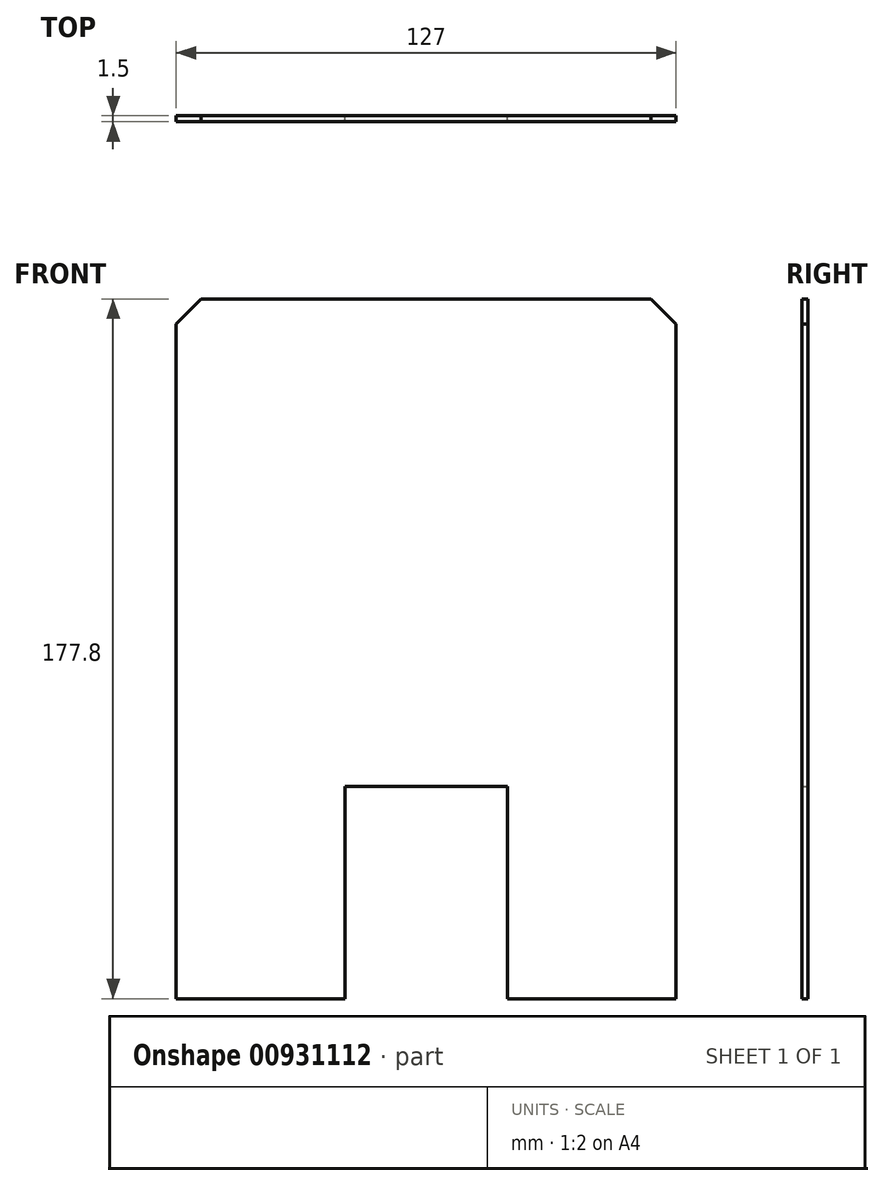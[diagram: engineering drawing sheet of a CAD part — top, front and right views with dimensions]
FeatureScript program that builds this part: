
annotation { "Feature Type Name" : "Feature", "Feature Type Description" : "" }
export const myFeature = defineFeature(function(context is Context, id is Id, definition is map)
    precondition{}
    {
        {
            var Q0;
            Q0=qCreatedBy(makeId("Front.planeOp"),FACE);
            var sketch = newSketch(context, id + "F0", { "sketchPlane" : qUnion([Q0])});
            skLineSegment(sketch, "E0.bottom", {"start": v(63.5, 88.9) * mm, "end": v(-63.5, 88.9) * mm});
            skLineSegment(sketch, "E0.top", {"start": v(63.5, -88.9) * mm, "end": v(20.64, -88.9) * mm});
            skLineSegment(sketch, "E0.left", {"start": v(63.5, 88.9) * mm, "end": v(63.5, -88.9) * mm});
            skLineSegment(sketch, "E0.right", {"start": v(-63.5, 88.9) * mm, "end": v(-63.5, -88.9) * mm});
            skPoint(sketch, "E0.middle", {"position": v(0, 0) * mm});
            skLineSegment(sketch, "E1.top", {"start": v(-20.64, -34.93) * mm, "end": v(20.64, -34.93) * mm});
            skLineSegment(sketch, "E1.left", {"start": v(-20.64, -88.9) * mm, "end": v(-20.64, -34.93) * mm});
            skLineSegment(sketch, "E1.right", {"start": v(20.64, -88.9) * mm, "end": v(20.64, -34.93) * mm});
            skLineSegment(sketch, "E2.trimOffspring", {"start": v(-20.64, -88.9) * mm, "end": v(-63.5, -88.9) * mm});
            skSolve(sketch);
        }
        {
            var Q0;
            Q0 = qSketchRegion(id + "F0", true);
            extrude(context, id + "F1", {"entities" : qUnion([Q0]), "endBound" : BoundingType.SYMMETRIC, "depth" : 1.5 * mm, "offsetDistance" : 25.4 * mm});
        }
        {
            var Q0;
            Q0=makeQuery(id+"F1.opExtrude","SWEPT_EDGE",EDGE,{"disambiguationData":[OSD([sQuery(id+"F0.wireOp",EDGE,"E0.bottom"),sQuery(id+"F0.wireOp",EDGE,"E0.left")])]});
            var Q1;
            Q1=makeQuery(id+"F1.opExtrude","SWEPT_EDGE",EDGE,{"disambiguationData":[OSD([sQuery(id+"F0.wireOp",EDGE,"E0.bottom"),sQuery(id+"F0.wireOp",EDGE,"E0.right")])]});
            chamfer(context, id + "F2", {"entities" : qUnion([Q0, Q1]), "width" : 6.35 * mm, "tangentPropagation" : true});
        }
    });
